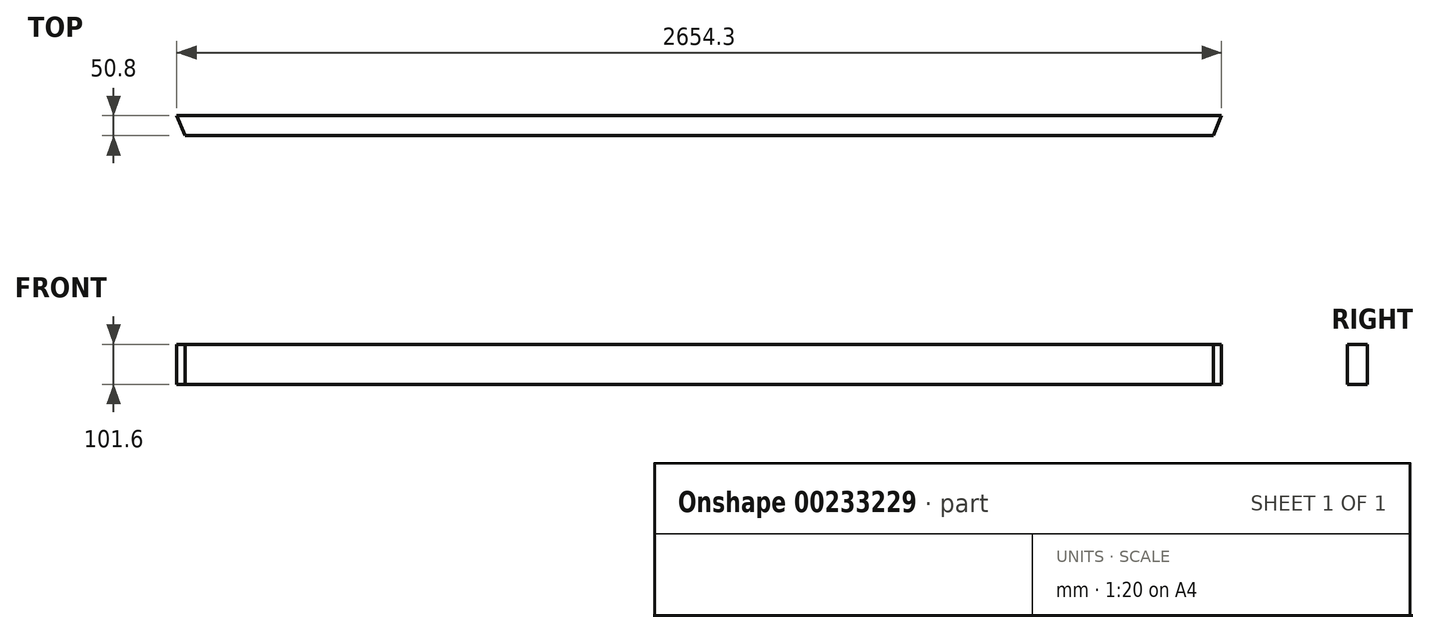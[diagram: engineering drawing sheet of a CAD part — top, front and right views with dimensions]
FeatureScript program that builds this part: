
annotation { "Feature Type Name" : "Feature", "Feature Type Description" : "" }
export const myFeature = defineFeature(function(context is Context, id is Id, definition is map)
    precondition{}
    {
        {
            var Q0;
            Q0=qCreatedBy(makeId("Front.planeOp"),FACE);
            var sketch = newSketch(context, id + "F0", { "sketchPlane" : qUnion([Q0])});
            skLineSegment(sketch, "E0.bottom", {"start": v(-1313.98, -977.46) * mm, "end": v(1340.32, -977.46) * mm});
            skLineSegment(sketch, "E0.top", {"start": v(-1313.98, -1079.06) * mm, "end": v(1340.32, -1079.06) * mm});
            skLineSegment(sketch, "E0.left", {"start": v(-1313.98, -977.46) * mm, "end": v(-1313.98, -1079.06) * mm});
            skLineSegment(sketch, "E0.right", {"start": v(1340.32, -977.46) * mm, "end": v(1340.32, -1079.06) * mm});
            skSolve(sketch);
        }
        {
            var Q0;
            Q0 = qSketchRegion(id + "F0", true);
            var Q1;
            Q1 = qSketchRegion(id + "F2", true);
            extrude(context, id + "F1", {"entities" : qUnion([Q0, Q1]), "depth" : 50.8 * mm});
        }
        {
            var Q0;
            Q0=makeQuery(id+"F1.opExtrude","SWEPT_FACE",FACE,{"disambiguationData":[OSD([sQuery(id+"F0.wireOp",EDGE,"E0.top")])]});
            var sketch = newSketch(context, id + "F2", { "sketchPlane" : qUnion([Q0])});
            skLineSegment(sketch, "E1", {"start": v(-1313.98, 50.8) * mm, "end": v(-1313.98, 0) * mm});
            skLineSegment(sketch, "E2", {"start": v(-1313.98, 0) * mm, "end": v(-1292.94, 50.8) * mm});
            skLineSegment(sketch, "E3", {"start": v(-1292.94, 50.8) * mm, "end": v(-1313.98, 50.8) * mm});
            skLineSegment(sketch, "E4", {"start": v(1340.32, 50.8) * mm, "end": v(1340.32, 0) * mm});
            skLineSegment(sketch, "E5", {"start": v(1340.32, 0) * mm, "end": v(1319.27, 50.8) * mm});
            skLineSegment(sketch, "E6", {"start": v(1319.27, 50.8) * mm, "end": v(1340.32, 50.8) * mm});
            skSolve(sketch);
        }
        {
            var Q0;
            Q0 = qSketchRegion(id + "F2", true);
            extrude(context, id + "F3", {"entities" : qUnion([Q0]), "operationType" : NewBodyOperationType.REMOVE, "oppositeDirection" : true, "depth" : 163.07 * mm});
        }
    });
